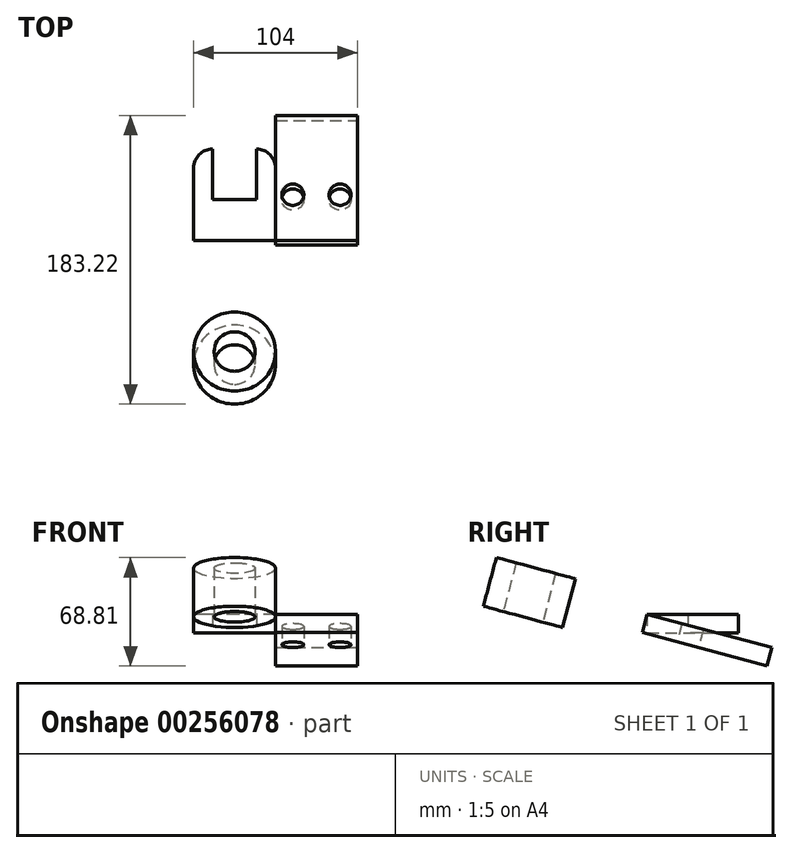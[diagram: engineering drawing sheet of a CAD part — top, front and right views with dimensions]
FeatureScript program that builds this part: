
annotation { "Feature Type Name" : "Feature", "Feature Type Description" : "" }
export const myFeature = defineFeature(function(context is Context, id is Id, definition is map)
    precondition{}
    {
        {
            var Q0;
            Q0=qCreatedBy(makeId("Top.planeOp"),FACE);
            var sketch = newSketch(context, id + "F0", { "sketchPlane" : qUnion([Q0])});
            skLineSegment(sketch, "E0", {"start": v(0, 0) * mm, "end": v(0, 25.45) * mm, "construction": true});
            skLineSegment(sketch, "E1", {"start": v(0, 0) * mm, "end": v(-26, 0) * mm});
            skLineSegment(sketch, "E2", {"start": v(-26, 0) * mm, "end": v(-26, 46) * mm});
            skLineSegment(sketch, "E3", {"start": v(-14, 58) * mm, "end": v(-14, 58) * mm});
            skLineSegment(sketch, "E4", {"start": v(-14, 58) * mm, "end": v(-14, 26) * mm});
            skLineSegment(sketch, "E5", {"start": v(-14, 26) * mm, "end": v(0, 26) * mm});
            skLineSegment(sketch, "E6", {"start": v(0, 25.45) * mm, "end": v(0, 45.18) * mm, "construction": true});
            skPoint(sketch, "E7.visualSharp", {"position": v(-26, 58) * mm});
            skArc(sketch, "E7.filletArc", {"start": v(-14, 58) * mm, "mid": v(-22.49, 54.49) * mm, "end": v(-26, 46) * mm});
            skLineSegment(sketch, "E8.MirrorCS", {"start": v(14, 26) * mm, "end": v(0, 26) * mm});
            skLineSegment(sketch, "E9.MirrorCS", {"start": v(14, 58) * mm, "end": v(14, 26) * mm});
            skArc(sketch, "E10.MirrorCS", {"start": v(14, 58) * mm, "mid": v(22.49, 54.49) * mm, "end": v(26, 46) * mm});
            skLineSegment(sketch, "E11.MirrorCS", {"start": v(26, 0) * mm, "end": v(26, 46) * mm});
            skLineSegment(sketch, "E12.MirrorCS", {"start": v(0, 0) * mm, "end": v(26, 0) * mm});
            skSolve(sketch);
        }
        {
            var Q0;
            Q0=makeQuery(id+"F0.imprint","IMPRINT",FACE,{"disambiguationData":[TD([[makeQuery(id+"F0.imprint","IMPRINT",EDGE,{"derivedFrom":sQuery(id+"F0.wireOp",EDGE,"E1")}),-1.0]])]});
            extrude(context, id + "F1", {"entities" : qUnion([Q0]), "depth" : 12 * mm});
        }
        {
            var Q0;
            Q0=makeQuery(id+"F1.opExtrude","CAP_EDGE",EDGE,{"disambiguationData":[OSD([sQuery(id+"F0.wireOp",EDGE,"E1"),sQuery(id+"F0.wireOp",EDGE,"E12.MirrorCS")])],"isStart":true});
            cPlane(context, id + "F2", {"entities" : qUnion([Q0]), "cplaneType" : CPlaneType.LINE_ANGLE, "offset" : 25 * mm, "angle" : 45 * degree, "oppositeDirection" : true, "width" : 150 * mm, "height" : 150 * mm});
        }
        {
            var Q0;
            Q0=qCreatedBy(id+"F2.planeOp",FACE);
            var sketch = newSketch(context, id + "F3", { "sketchPlane" : qUnion([Q0])});
            skLineSegment(sketch, "E13", {"start": v(0, 0) * mm, "end": v(26, 0) * mm});
            skLineSegment(sketch, "E14", {"start": v(26, 0) * mm, "end": v(26, -82) * mm});
            skLineSegment(sketch, "E15", {"start": v(26, -82) * mm, "end": v(0, -82) * mm});
            skLineSegment(sketch, "E16", {"start": v(0, 0) * mm, "end": v(0, -82) * mm, "construction": true});
            skLineSegment(sketch, "E17", {"start": v(0, 0) * mm, "end": v(0, -30) * mm, "construction": true});
            skLineSegment(sketch, "E18", {"start": v(0, -30) * mm, "end": v(26, -30) * mm, "construction": true});
            skCircle(sketch, "E19", {"center": v(0, -30) * mm, "radius": 15 * mm, "construction": true});
            skCircle(sketch, "E20", {"center": v(15, -30) * mm, "radius": 7 * mm});
            skCircle(sketch, "E21.MirrorC", {"center": v(-15, -30) * mm, "radius": 7 * mm});
            skLineSegment(sketch, "E22.MirrorCS", {"start": v(-26, 0) * mm, "end": v(-26, -82) * mm});
            skLineSegment(sketch, "E23.MirrorCS", {"start": v(-26, -82) * mm, "end": v(0, -82) * mm});
            skLineSegment(sketch, "E24", {"start": v(0, 0) * mm, "end": v(-26, 0) * mm});
            skSolve(sketch);
        }
        {
            var Q0;
            Q0 = qSketchRegion(id + "F3", true);
            extrude(context, id + "F4", {"entities" : qUnion([Q0]), "oppositeDirection" : true, "depth" : 12 * mm});
        }
        {
            var Q0;
            Q0=makeQuery(id+"F4.opExtrude","SWEPT_BODY",BODY,{"disambiguationData":[OSD([sQuery(id+"F3.wireOp",EDGE,"E13"),sQuery(id+"F3.wireOp",EDGE,"E14"),sQuery(id+"F3.wireOp",EDGE,"E15"),sQuery(id+"F3.wireOp",EDGE,"E20"),sQuery(id+"F3.wireOp",EDGE,"E21.MirrorC"),sQuery(id+"F3.wireOp",EDGE,"E22.MirrorCS"),sQuery(id+"F3.wireOp",EDGE,"E23.MirrorCS"),sQuery(id+"F3.wireOp",EDGE,"E24")])]});
            var Q1;
            Q1=makeQuery(id+"F1.opExtrude","CAP_VERTEX",VERTEX,{"disambiguationData":[OSD([sQuery(id+"F0.wireOp",EDGE,"E11.MirrorCS"),sQuery(id+"F0.wireOp",EDGE,"E12.MirrorCS")])],"isStart":false});
            var Q2;
            Q2=makeQuery(id+"F4.opExtrude","CAP_VERTEX",VERTEX,{"disambiguationData":[OSD([sQuery(id+"F3.wireOp",EDGE,"E22.MirrorCS"),sQuery(id+"F3.wireOp",EDGE,"E24")])],"isStart":false});
            transform(context, id + "F5", {"entities" : qUnion([Q0]), "transformType" : TransformType.TRANSLATION_ENTITY, "oppositeDirectionEntity" : true, "transformLine" : qUnion([Q1, Q2]), "makeCopy" : false});
        }
        {
            var Q0;
            Q0=makeQuery(id+"F4.opExtrude","SWEPT_BODY",BODY,{"disambiguationData":[OSD([sQuery(id+"F3.wireOp",EDGE,"E13"),sQuery(id+"F3.wireOp",EDGE,"E14"),sQuery(id+"F3.wireOp",EDGE,"E15"),sQuery(id+"F3.wireOp",EDGE,"E20"),sQuery(id+"F3.wireOp",EDGE,"E21.MirrorC"),sQuery(id+"F3.wireOp",EDGE,"E22.MirrorCS"),sQuery(id+"F3.wireOp",EDGE,"E23.MirrorCS"),sQuery(id+"F3.wireOp",EDGE,"E24")])]});
            var Q1;
            Q1=makeQuery(id+"F1.opExtrude","CAP_EDGE",EDGE,{"disambiguationData":[OSD([sQuery(id+"F0.wireOp",EDGE,"E1"),sQuery(id+"F0.wireOp",EDGE,"E12.MirrorCS")])],"isStart":false});
            transform(context, id + "F6", {"entities" : qUnion([Q0]), "transformType" : TransformType.ROTATION, "transformAxis" : qUnion([Q1]), "angle" : 30 * degree, "oppositeDirection" : true, "makeCopy" : false});
        }
        {
            var Q0;
            Q0=makeQuery(id+"F4.opExtrude","CAP_FACE",FACE,{"disambiguationData":[OSD([sQuery(id+"F3.wireOp",EDGE,"E13"),sQuery(id+"F3.wireOp",EDGE,"E14"),sQuery(id+"F3.wireOp",EDGE,"E15"),sQuery(id+"F3.wireOp",EDGE,"E20"),sQuery(id+"F3.wireOp",EDGE,"E21.MirrorC"),sQuery(id+"F3.wireOp",EDGE,"E22.MirrorCS"),sQuery(id+"F3.wireOp",EDGE,"E23.MirrorCS"),sQuery(id+"F3.wireOp",EDGE,"E24")])],"isStart":false});
            var sketch = newSketch(context, id + "F7", { "sketchPlane" : qUnion([Q0])});
            skLineSegment(sketch, "E25", {"start": v(0, -78.9) * mm, "end": v(0, -132.5) * mm, "construction": true});
            skCircle(sketch, "E26", {"center": v(0, -78.9) * mm, "radius": 26 * mm});
            skCircle(sketch, "E27", {"center": v(0, -78.9) * mm, "radius": 13 * mm});
            skSolve(sketch);
        }
        {
            var Q0;
            {var subQ0=sQuery(id+"F7.wireOp",EDGE,"E27");var subQ1=makeQuery(id+"F4.opExtrude","CAP_EDGE",EDGE,{"disambiguationData":[OSD([sQuery(id+"F3.wireOp",EDGE,"E15"),sQuery(id+"F3.wireOp",EDGE,"E23.MirrorCS")])],"isStart":false});var subQ2=makeQuery(id+"F7.imprint","INTERSECT",VERTEX,{"disambiguationData":[OD(0.0)],"derivedFrom":[subQ1,subQ0]});Q0=makeQuery(id+"F7.imprint","IMPRINT",FACE,{"disambiguationData":[TD([[makeQuery(id+"F7.imprint","IMPRINT",EDGE,{"disambiguationData":[TD([[subQ2,1.0]])],"derivedFrom":subQ0}),1.0]])]});}
            var Q1;
            {var subQ0=sQuery(id+"F7.wireOp",EDGE,"E27");var subQ1=makeQuery(id+"F4.opExtrude","CAP_EDGE",EDGE,{"disambiguationData":[OSD([sQuery(id+"F3.wireOp",EDGE,"E15"),sQuery(id+"F3.wireOp",EDGE,"E23.MirrorCS")])],"isStart":false});var subQ2=makeQuery(id+"F7.imprint","INTERSECT",VERTEX,{"disambiguationData":[OD(0.0)],"derivedFrom":[subQ1,subQ0]});Q1=makeQuery(id+"F7.imprint","IMPRINT",FACE,{"disambiguationData":[TD([[makeQuery(id+"F7.imprint","IMPRINT",EDGE,{"disambiguationData":[TD([[subQ2,-1.0]])],"derivedFrom":subQ0}),1.0]])]});}
            extrude(context, id + "F8", {"entities" : qUnion([Q0, Q1]), "oppositeDirection" : true, "depth" : 25 * mm});
        }
        {
            var Q0;
            {var subQ1=makeQuery(id+"F4.opExtrude","CAP_EDGE",EDGE,{"disambiguationData":[OSD([sQuery(id+"F3.wireOp",EDGE,"E15"),sQuery(id+"F3.wireOp",EDGE,"E23.MirrorCS")])],"isStart":false});var subQ4=sQuery(id+"F7.wireOp",EDGE,"E27");var subQ5=makeQuery(id+"F7.imprint","INTERSECT",VERTEX,{"disambiguationData":[OD(0.0)],"derivedFrom":[subQ1,subQ4]});Q0=makeQuery(id+"F7.imprint","IMPRINT",FACE,{"disambiguationData":[TD([[makeQuery(id+"F7.imprint","IMPRINT",EDGE,{"disambiguationData":[TD([[subQ5,1.0]])],"derivedFrom":subQ4}),-1.0]])]});}
            var Q1;
            {var subQ1=makeQuery(id+"F4.opExtrude","CAP_EDGE",EDGE,{"disambiguationData":[OSD([sQuery(id+"F3.wireOp",EDGE,"E15"),sQuery(id+"F3.wireOp",EDGE,"E23.MirrorCS")])],"isStart":false});var subQ4=sQuery(id+"F7.wireOp",EDGE,"E27");var subQ5=makeQuery(id+"F7.imprint","INTERSECT",VERTEX,{"disambiguationData":[OD(0.0)],"derivedFrom":[subQ1,subQ4]});Q1=makeQuery(id+"F7.imprint","IMPRINT",FACE,{"disambiguationData":[TD([[makeQuery(id+"F7.imprint","IMPRINT",EDGE,{"disambiguationData":[TD([[subQ5,-1.0]])],"derivedFrom":subQ4}),-1.0]])]});}
            extrude(context, id + "F9", {"entities" : qUnion([Q0, Q1]), "depth" : 10 * mm, "hasSecondDirection" : true, "secondDirectionOppositeDirection" : true, "secondDirectionDepth" : 22 * mm});
        }
        {
            var Q0;
            Q0=makeQuery(id+"F8.opExtrude","SWEPT_BODY",BODY,{"disambiguationData":[OSD([sQuery(id+"F7.wireOp",EDGE,"E27")])]});
            var Q1;
            Q1=makeQuery(id+"F4.opExtrude","SWEPT_BODY",BODY,{"disambiguationData":[OSD([sQuery(id+"F3.wireOp",EDGE,"E13"),sQuery(id+"F3.wireOp",EDGE,"E14"),sQuery(id+"F3.wireOp",EDGE,"E15"),sQuery(id+"F3.wireOp",EDGE,"E20"),sQuery(id+"F3.wireOp",EDGE,"E21.MirrorC"),sQuery(id+"F3.wireOp",EDGE,"E22.MirrorCS"),sQuery(id+"F3.wireOp",EDGE,"E23.MirrorCS"),sQuery(id+"F3.wireOp",EDGE,"E24")])]});
            booleanBodies(context, id + "F10", {"operationType" : BooleanOperationType.SUBTRACTION, "tools" : qUnion([Q0]), "targets" : qUnion([Q1])});
        }
    });
